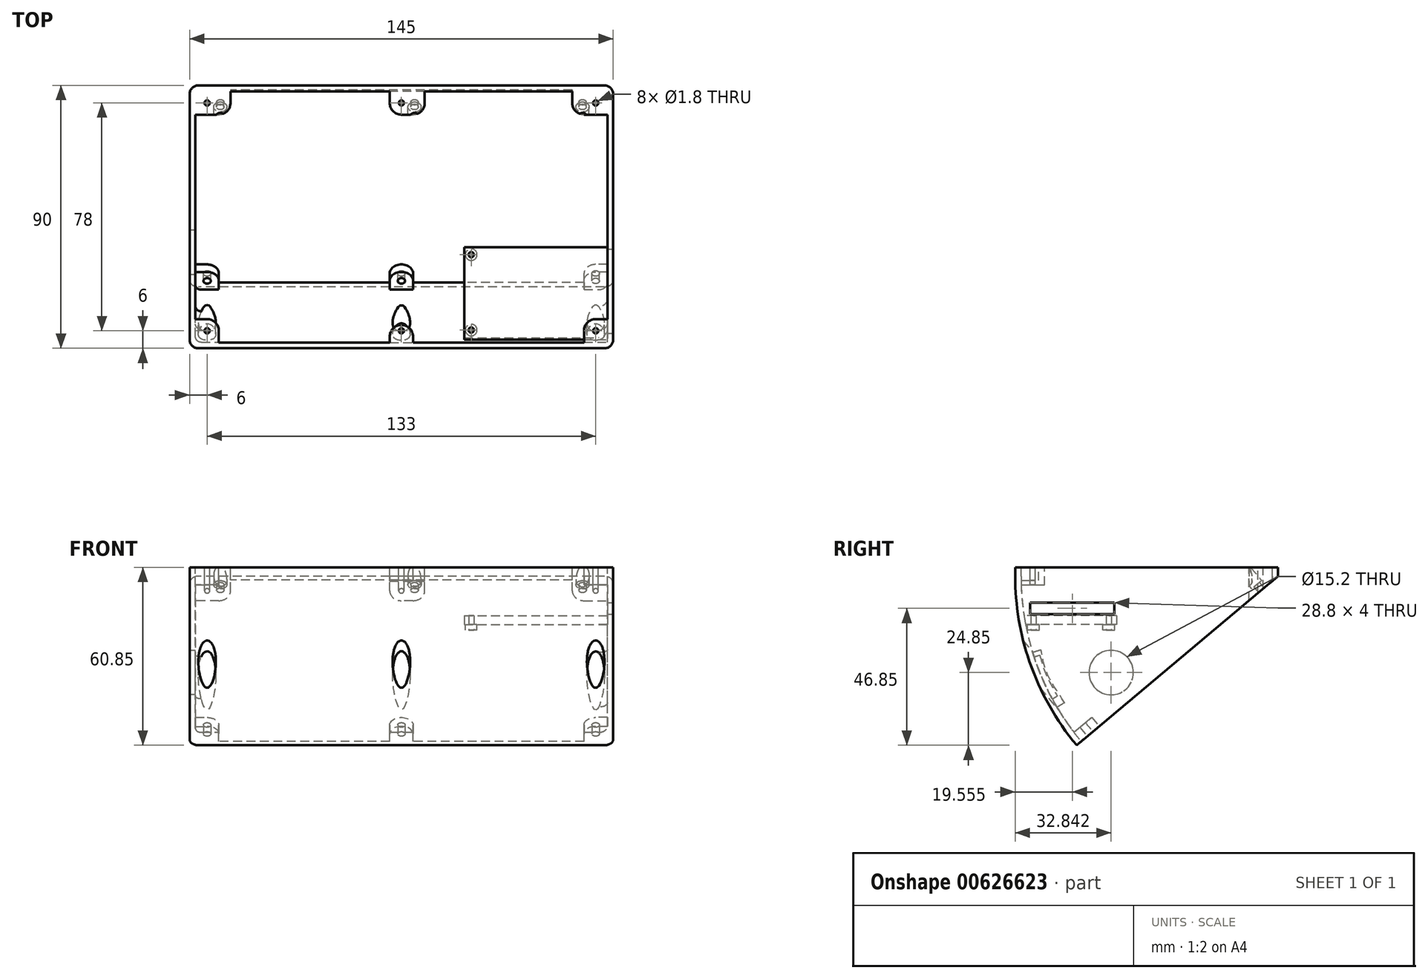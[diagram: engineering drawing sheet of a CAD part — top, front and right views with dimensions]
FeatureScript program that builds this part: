
annotation { "Feature Type Name" : "Feature", "Feature Type Description" : "" }
export const myFeature = defineFeature(function(context is Context, id is Id, definition is map)
    precondition{}
    {
        {
            var Q0;
            Q0=qCreatedBy(makeId("Top.planeOp"),FACE);
            var sketch = newSketch(context, id + "F0", { "sketchPlane" : qUnion([Q0])});
            skLineSegment(sketch, "E0.bottom", {"start": v(72.5, -45) * mm, "end": v(-72.5, -45) * mm});
            skLineSegment(sketch, "E0.top", {"start": v(72.5, 45) * mm, "end": v(-72.5, 45) * mm});
            skLineSegment(sketch, "E0.left", {"start": v(72.5, -45) * mm, "end": v(72.5, 45) * mm});
            skLineSegment(sketch, "E0.right", {"start": v(-72.5, -45) * mm, "end": v(-72.5, 45) * mm});
            skPoint(sketch, "E0.middle", {"position": v(0, 0) * mm});
            skLineSegment(sketch, "E1.bottom", {"start": v(70.5, -43) * mm, "end": v(-70.5, -43) * mm});
            skLineSegment(sketch, "E1.top", {"start": v(70.5, 43) * mm, "end": v(-70.5, 43) * mm});
            skLineSegment(sketch, "E1.left", {"start": v(70.5, -43) * mm, "end": v(70.5, 43) * mm});
            skLineSegment(sketch, "E1.right", {"start": v(-70.5, -43) * mm, "end": v(-70.5, 43) * mm});
            skSolve(sketch);
        }
        {
            var Q0;
            Q0=qCreatedBy(makeId("Right.planeOp"),FACE);
            cPlane(context, id + "F1", {"entities" : qUnion([Q0]), "cplaneType" : CPlaneType.OFFSET, "offset" : 75 * mm, "width" : 150 * mm, "height" : 150 * mm});
        }
        {
            var Q0;
            Q0=qCreatedBy(id+"F1.planeOp",FACE);
            var sketch = newSketch(context, id + "F2", { "sketchPlane" : qUnion([Q0])});
            skLineSegment(sketch, "E2", {"start": v(45, 0) * mm, "end": v(-16.28, -51.42) * mm, "construction": true});
            skArc(sketch, "E3", {"start": v(-35, 0) * mm, "mid": v(-30.18, -27.36) * mm, "end": v(-16.28, -51.42) * mm});
            skSolve(sketch);
        }
        {
            var Q0;
            Q0=makeQuery(id+"F0.imprint","IMPRINT",FACE,{"disambiguationData":[TD([[makeQuery(id+"F0.imprint","IMPRINT",EDGE,{"derivedFrom":sQuery(id+"F0.wireOp",EDGE,"E0.bottom")}),-1.0]])]});
            var Q1;
            Q1=sQuery(id+"F2.wireOp",EDGE,"E3");
            sweep(context, id + "F3", {"profiles" : qUnion([Q0]), "path" : qUnion([Q1])});
        }
        {
            var Q0;
            Q0=makeQuery(id+"F3.opSweep","CAP_FACE",FACE,{"disambiguationData":[OSD([sQuery(id+"F0.wireOp",EDGE,"E0.bottom"),sQuery(id+"F0.wireOp",EDGE,"E0.top"),sQuery(id+"F0.wireOp",EDGE,"E0.left"),sQuery(id+"F0.wireOp",EDGE,"E0.right"),sQuery(id+"F0.wireOp",EDGE,"E1.bottom"),sQuery(id+"F0.wireOp",EDGE,"E1.top"),sQuery(id+"F0.wireOp",EDGE,"E1.left"),sQuery(id+"F0.wireOp",EDGE,"E1.right"),sQuery(id+"F2.wireOp",VERTEX,"E3.start")])],"isStart":true});
            extrude(context, id + "F4", {"entities" : qUnion([Q0]), "operationType" : NewBodyOperationType.ADD, "depth" : 3 * mm});
        }
        {
            var Q0;
            {var subQ0=sQuery(id+"F0.wireOp",EDGE,"E0.right");Q0=makeQuery(id+"F4.boolean.opBoolean","MERGE",FACE,{"derivedFrom":[makeQuery(id+"F3.opSweep","SWEPT_FACE",FACE,{"disambiguationData":[OSD([subQ0,sQuery(id+"F2.wireOp",EDGE,"E3")])]}),makeQuery(id+"F4.opExtrude","SWEPT_FACE",FACE,{"disambiguationData":[OSD([subQ0,sQuery(id+"F2.wireOp",VERTEX,"E3.start")])]})]});}
            var sketch = newSketch(context, id + "F5", { "sketchPlane" : qUnion([Q0])});
            skCircle(sketch, "E4", {"center": v(12.16, -33) * mm, "radius": 7.6 * mm});
            skLineSegment(sketch, "E5", {"start": v(-45, 0) * mm, "end": v(12.16, -33) * mm, "construction": true});
            skCircle(sketch, "E6", {"center": v(12.16, -33) * mm, "radius": 9.5 * mm, "construction": true});
            skSolve(sketch);
        }
        {
            var Q0;
            Q0=makeQuery(id+"F5.imprint","IMPRINT",FACE,{"disambiguationData":[TD([[makeQuery(id+"F5.imprint","IMPRINT",EDGE,{"derivedFrom":sQuery(id+"F5.wireOp",EDGE,"E4")}),1.0]])]});
            extrude(context, id + "F6", {"entities" : qUnion([Q0]), "operationType" : NewBodyOperationType.REMOVE, "endBound" : BoundingType.UP_TO_NEXT, "oppositeDirection" : true, "depth" : 25 * mm});
        }
        {
            var Q0;
            {var subQ0=sQuery(id+"F0.wireOp",EDGE,"E0.left");Q0=makeQuery(id+"F4.boolean.opBoolean","MERGE",FACE,{"derivedFrom":[makeQuery(id+"F3.opSweep","SWEPT_FACE",FACE,{"disambiguationData":[OSD([subQ0,sQuery(id+"F2.wireOp",EDGE,"E3")])]}),makeQuery(id+"F4.opExtrude","SWEPT_FACE",FACE,{"disambiguationData":[OSD([subQ0,sQuery(id+"F2.wireOp",VERTEX,"E3.start")])]})]});}
            var sketch = newSketch(context, id + "F7", { "sketchPlane" : qUnion([Q0])});
            skLineSegment(sketch, "E7.bottom", {"start": v(-39.84, -9) * mm, "end": v(-11.04, -9) * mm});
            skLineSegment(sketch, "E7.top", {"start": v(-39.84, -13) * mm, "end": v(-11.04, -13) * mm});
            skLineSegment(sketch, "E7.left", {"start": v(-39.84, -9) * mm, "end": v(-39.84, -13) * mm});
            skLineSegment(sketch, "E7.right", {"start": v(-11.04, -9) * mm, "end": v(-11.04, -13) * mm});
            skPoint(sketch, "E8", {"position": v(-25.44, -9) * mm});
            skSolve(sketch);
        }
        {
            var Q0;
            Q0=makeQuery(id+"F7.imprint","IMPRINT",FACE,{"disambiguationData":[TD([[makeQuery(id+"F7.imprint","IMPRINT",EDGE,{"derivedFrom":sQuery(id+"F7.wireOp",EDGE,"E7.bottom")}),-1.0]])]});
            extrude(context, id + "F8", {"entities" : qUnion([Q0]), "operationType" : NewBodyOperationType.REMOVE, "endBound" : BoundingType.UP_TO_NEXT, "oppositeDirection" : true, "depth" : 25 * mm});
        }
        {
            var Q0;
            {var subQ0=sQuery(id+"F0.wireOp",EDGE,"E1.left");Q0=makeQuery(id+"F4.boolean.opBoolean","MERGE",FACE,{"derivedFrom":[makeQuery(id+"F3.opSweep","SWEPT_FACE",FACE,{"disambiguationData":[OSD([subQ0,sQuery(id+"F2.wireOp",EDGE,"E3")])]}),makeQuery(id+"F4.opExtrude","SWEPT_FACE",FACE,{"disambiguationData":[OSD([subQ0,sQuery(id+"F2.wireOp",VERTEX,"E3.start")])]})]});}
            var sketch = newSketch(context, id + "F9", { "sketchPlane" : qUnion([Q0])});
            skLineSegment(sketch, "E9.bottom", {"start": v(10.34, -13.5) * mm, "end": v(41.34, -13.5) * mm});
            skLineSegment(sketch, "E9.top", {"start": v(10.34, -16.5) * mm, "end": v(41.34, -16.5) * mm});
            skLineSegment(sketch, "E9.left", {"start": v(10.34, -13.5) * mm, "end": v(10.34, -16.5) * mm});
            skLineSegment(sketch, "E9.right", {"start": v(41.34, -13.5) * mm, "end": v(41.34, -16.5) * mm});
            skPoint(sketch, "E10", {"position": v(25.84, -13.5) * mm});
            skSolve(sketch);
        }
        {
            var Q0;
            Q0=makeQuery(id+"F9.imprint","IMPRINT",FACE,{"disambiguationData":[TD([[makeQuery(id+"F9.imprint","IMPRINT",EDGE,{"derivedFrom":sQuery(id+"F9.wireOp",EDGE,"E9.top")}),1.0]])]});
            extrude(context, id + "F10", {"entities" : qUnion([Q0]), "operationType" : NewBodyOperationType.ADD, "depth" : 49 * mm});
        }
        {
            var Q0;
            Q0=makeQuery(id+"F10.opExtrude","SWEPT_FACE",FACE,{"disambiguationData":[OSD([sQuery(id+"F9.wireOp",EDGE,"E9.top")])]});
            var sketch = newSketch(context, id + "F11", { "sketchPlane" : qUnion([Q0])});
            skCircle(sketch, "E11", {"center": v(23.9, 12.94) * mm, "radius": 0.9 * mm});
            skCircle(sketch, "E12", {"center": v(23.9, 38.74) * mm, "radius": 0.9 * mm});
            skLineSegment(sketch, "E13", {"start": v(21.5, 25.84) * mm, "end": v(33.65, 25.84) * mm, "construction": true});
            skCircle(sketch, "E14", {"center": v(23.9, 12.94) * mm, "radius": 2 * mm});
            skCircle(sketch, "E15", {"center": v(23.9, 38.74) * mm, "radius": 2 * mm});
            skSolve(sketch);
        }
        {
            var Q0;
            Q0=makeQuery(id+"F11.imprint","IMPRINT",FACE,{"disambiguationData":[TD([[makeQuery(id+"F11.imprint","IMPRINT",EDGE,{"derivedFrom":sQuery(id+"F11.wireOp",EDGE,"E12")}),1.0]])]});
            var Q1;
            Q1=makeQuery(id+"F11.imprint","IMPRINT",FACE,{"disambiguationData":[TD([[makeQuery(id+"F11.imprint","IMPRINT",EDGE,{"derivedFrom":sQuery(id+"F11.wireOp",EDGE,"E11")}),1.0]])]});
            extrude(context, id + "F12", {"entities" : qUnion([Q0, Q1]), "operationType" : NewBodyOperationType.REMOVE, "endBound" : BoundingType.UP_TO_NEXT, "oppositeDirection" : true, "depth" : 25 * mm});
        }
        {
            var Q0;
            Q0=makeQuery(id+"F11.imprint","IMPRINT",FACE,{"disambiguationData":[TD([[makeQuery(id+"F11.imprint","IMPRINT",EDGE,{"derivedFrom":sQuery(id+"F11.wireOp",EDGE,"E11")}),-1.0]])]});
            var Q1;
            Q1=makeQuery(id+"F11.imprint","IMPRINT",FACE,{"disambiguationData":[TD([[makeQuery(id+"F11.imprint","IMPRINT",EDGE,{"derivedFrom":sQuery(id+"F11.wireOp",EDGE,"E12")}),-1.0]])]});
            extrude(context, id + "F13", {"entities" : qUnion([Q0, Q1]), "operationType" : NewBodyOperationType.ADD, "depth" : 2 * mm});
        }
        {
            var Q0;
            Q0=makeQuery(id+"F10.opExtrude","SWEPT_FACE",FACE,{"disambiguationData":[OSD([sQuery(id+"F9.wireOp",EDGE,"E9.right")])]});
            var Q1;
            Q1=makeQuery(id+"F3.opSweep","SWEPT_FACE",FACE,{"disambiguationData":[OSD([sQuery(id+"F0.wireOp",EDGE,"E1.bottom"),sQuery(id+"F2.wireOp",EDGE,"E3")])]});
            extrude(context, id + "F14", {"entities" : qUnion([Q0]), "operationType" : NewBodyOperationType.ADD, "endBound" : BoundingType.UP_TO_SURFACE, "endBoundEntityFace" : qUnion([Q1]), "depth" : 25 * mm});
        }
        {
            var Q0;
            Q0=makeQuery(id+"F4.opExtrude","CAP_FACE",FACE,{"disambiguationData":[OSD([sQuery(id+"F0.wireOp",EDGE,"E0.bottom"),sQuery(id+"F0.wireOp",EDGE,"E0.top"),sQuery(id+"F0.wireOp",EDGE,"E0.left"),sQuery(id+"F0.wireOp",EDGE,"E0.right"),sQuery(id+"F0.wireOp",EDGE,"E1.bottom"),sQuery(id+"F0.wireOp",EDGE,"E1.top"),sQuery(id+"F0.wireOp",EDGE,"E1.left"),sQuery(id+"F0.wireOp",EDGE,"E1.right"),sQuery(id+"F2.wireOp",VERTEX,"E3.start")])],"isStart":false});
            var sketch = newSketch(context, id + "F15", { "sketchPlane" : qUnion([Q0])});
            skLineSegment(sketch, "E16.bottom", {"start": v(-70.5, -43) * mm, "end": v(-62.5, -43) * mm});
            skLineSegment(sketch, "E16.top", {"start": v(-70.5, -35) * mm, "end": v(-62.5, -35) * mm});
            skLineSegment(sketch, "E16.left", {"start": v(-70.5, -43) * mm, "end": v(-70.5, -35) * mm});
            skLineSegment(sketch, "E16.right", {"start": v(-62.5, -43) * mm, "end": v(-62.5, -35) * mm});
            skLineSegment(sketch, "E17.bottom", {"start": v(70.5, -43) * mm, "end": v(62.5, -43) * mm});
            skLineSegment(sketch, "E17.top", {"start": v(70.5, -35) * mm, "end": v(62.5, -35) * mm});
            skLineSegment(sketch, "E17.left", {"start": v(70.5, -43) * mm, "end": v(70.5, -35) * mm});
            skLineSegment(sketch, "E17.right", {"start": v(62.5, -43) * mm, "end": v(62.5, -35) * mm});
            skLineSegment(sketch, "E18.bottom", {"start": v(-70.5, 43) * mm, "end": v(-58.5, 43) * mm});
            skLineSegment(sketch, "E18.top", {"start": v(-70.5, 35) * mm, "end": v(-58.5, 35) * mm});
            skLineSegment(sketch, "E18.left", {"start": v(-70.5, 43) * mm, "end": v(-70.5, 35) * mm});
            skLineSegment(sketch, "E18.right", {"start": v(-58.5, 43) * mm, "end": v(-58.5, 35) * mm});
            skLineSegment(sketch, "E19.bottom", {"start": v(70.5, 43) * mm, "end": v(58.5, 43) * mm});
            skLineSegment(sketch, "E19.top", {"start": v(70.5, 35) * mm, "end": v(58.5, 35) * mm});
            skLineSegment(sketch, "E19.left", {"start": v(70.5, 43) * mm, "end": v(70.5, 35) * mm});
            skLineSegment(sketch, "E19.right", {"start": v(58.5, 43) * mm, "end": v(58.5, 35) * mm});
            skLineSegment(sketch, "E20.bottom", {"start": v(4, -43) * mm, "end": v(-4, -43) * mm});
            skLineSegment(sketch, "E20.top", {"start": v(4, -37) * mm, "end": v(-4, -37) * mm});
            skLineSegment(sketch, "E20.left", {"start": v(4, -43) * mm, "end": v(4, -37) * mm});
            skLineSegment(sketch, "E20.right", {"start": v(-4, -43) * mm, "end": v(-4, -37) * mm});
            skPoint(sketch, "E20.middle", {"position": v(0, -40) * mm});
            skLineSegment(sketch, "E21.bottom", {"start": v(-4, 43) * mm, "end": v(8, 43) * mm});
            skLineSegment(sketch, "E21.top", {"start": v(-4, 35) * mm, "end": v(8, 35) * mm});
            skLineSegment(sketch, "E21.left", {"start": v(-4, 43) * mm, "end": v(-4, 35) * mm});
            skLineSegment(sketch, "E21.right", {"start": v(8, 43) * mm, "end": v(8, 35) * mm});
            skSolve(sketch);
        }
        {
            var Q0;
            Q0=makeQuery(id+"F15.imprint","IMPRINT",FACE,{"disambiguationData":[TD([[makeQuery(id+"F15.imprint","IMPRINT",EDGE,{"derivedFrom":sQuery(id+"F15.wireOp",EDGE,"E16.bottom")}),-1.0]])]});
            var Q1;
            Q1=makeQuery(id+"F15.imprint","IMPRINT",FACE,{"disambiguationData":[TD([[makeQuery(id+"F15.imprint","IMPRINT",EDGE,{"derivedFrom":sQuery(id+"F15.wireOp",EDGE,"E17.bottom")}),-1.0]])]});
            extrude(context, id + "F16", {"entities" : qUnion([Q0, Q1]), "operationType" : NewBodyOperationType.ADD, "oppositeDirection" : true, "depth" : 6 * mm});
        }
        {
            var Q0;
            Q0=makeQuery(id+"F15.imprint","IMPRINT",FACE,{"disambiguationData":[TD([[makeQuery(id+"F15.imprint","IMPRINT",EDGE,{"derivedFrom":sQuery(id+"F15.wireOp",EDGE,"E20.bottom")}),-1.0]])]});
            extrude(context, id + "F17", {"entities" : qUnion([Q0]), "operationType" : NewBodyOperationType.ADD, "oppositeDirection" : true, "depth" : 4.5 * mm});
        }
        {
            var Q0;
            Q0=makeQuery(id+"F15.imprint","IMPRINT",FACE,{"disambiguationData":[TD([[makeQuery(id+"F15.imprint","IMPRINT",EDGE,{"derivedFrom":sQuery(id+"F15.wireOp",EDGE,"E18.bottom")}),1.0]])]});
            var Q1;
            Q1=makeQuery(id+"F15.imprint","IMPRINT",FACE,{"disambiguationData":[TD([[makeQuery(id+"F15.imprint","IMPRINT",EDGE,{"derivedFrom":sQuery(id+"F15.wireOp",EDGE,"E19.bottom")}),1.0]])]});
            var Q2;
            Q2=makeQuery(id+"F15.imprint","IMPRINT",FACE,{"disambiguationData":[TD([[makeQuery(id+"F15.imprint","IMPRINT",EDGE,{"derivedFrom":sQuery(id+"F15.wireOp",EDGE,"E21.bottom")}),1.0]])]});
            var Q3;
            Q3=makeQuery(id+"F3.opSweep","CAP_FACE",FACE,{"disambiguationData":[OSD([sQuery(id+"F0.wireOp",EDGE,"E0.bottom"),sQuery(id+"F0.wireOp",EDGE,"E0.top"),sQuery(id+"F0.wireOp",EDGE,"E0.left"),sQuery(id+"F0.wireOp",EDGE,"E0.right"),sQuery(id+"F0.wireOp",EDGE,"E1.bottom"),sQuery(id+"F0.wireOp",EDGE,"E1.top"),sQuery(id+"F0.wireOp",EDGE,"E1.left"),sQuery(id+"F0.wireOp",EDGE,"E1.right"),sQuery(id+"F2.wireOp",VERTEX,"E3.end")])],"isStart":false});
            extrude(context, id + "F18", {"entities" : qUnion([Q0, Q1, Q2]), "operationType" : NewBodyOperationType.ADD, "endBound" : BoundingType.UP_TO_SURFACE, "oppositeDirection" : true, "endBoundEntityFace" : qUnion([Q3]), "depth" : 25 * mm});
        }
        {
            var Q0;
            {var subQ2=sQuery(id+"F0.wireOp",EDGE,"E1.left");var subQ9=sQuery(id+"F15.wireOp",EDGE,"E19.bottom");var subQ10=sQuery(id+"F2.wireOp",EDGE,"E3");Q0=makeQuery(id+"F18.boolean.opBoolean","SPLIT",FACE,{"disambiguationData":[TD([makeQuery(id+"F18.opExtrude","SWEPT_FACE",FACE,{"disambiguationData":[OSD([subQ9])]})])],"derivedFrom":makeQuery(id+"F4.boolean.opBoolean","MERGE",FACE,{"derivedFrom":[makeQuery(id+"F3.opSweep","SWEPT_FACE",FACE,{"disambiguationData":[OSD([subQ2,subQ10])]}),makeQuery(id+"F4.opExtrude","SWEPT_FACE",FACE,{"disambiguationData":[OSD([subQ2,sQuery(id+"F2.wireOp",VERTEX,"E3.start")])]})]})});}
            var Q1;
            Q1=makeQuery(id+"F18.opExtrude","SWEPT_FACE",FACE,{"disambiguationData":[OSD([sQuery(id+"F15.wireOp",EDGE,"E19.right")])]});
            extrude(context, id + "F19", {"entities" : qUnion([Q0]), "operationType" : NewBodyOperationType.ADD, "endBound" : BoundingType.UP_TO_SURFACE, "endBoundEntityFace" : qUnion([Q1]), "depth" : 25 * mm});
        }
        {
            var Q0;
            {var subQ0=sQuery(id+"F15.wireOp",EDGE,"E18.bottom");var subQ2=sQuery(id+"F0.wireOp",EDGE,"E1.right");var subQ10=sQuery(id+"F2.wireOp",EDGE,"E3");Q0=makeQuery(id+"F18.boolean.opBoolean","SPLIT",FACE,{"disambiguationData":[TD([makeQuery(id+"F18.opExtrude","SWEPT_FACE",FACE,{"disambiguationData":[OSD([subQ0])]})])],"derivedFrom":makeQuery(id+"F4.boolean.opBoolean","MERGE",FACE,{"derivedFrom":[makeQuery(id+"F3.opSweep","SWEPT_FACE",FACE,{"disambiguationData":[OSD([subQ2,subQ10])]}),makeQuery(id+"F4.opExtrude","SWEPT_FACE",FACE,{"disambiguationData":[OSD([subQ2,sQuery(id+"F2.wireOp",VERTEX,"E3.start")])]})]})});}
            var Q1;
            Q1=makeQuery(id+"F18.opExtrude","SWEPT_FACE",FACE,{"disambiguationData":[OSD([sQuery(id+"F15.wireOp",EDGE,"E18.right")])]});
            extrude(context, id + "F20", {"entities" : qUnion([Q0]), "operationType" : NewBodyOperationType.ADD, "endBound" : BoundingType.UP_TO_SURFACE, "endBoundEntityFace" : qUnion([Q1]), "depth" : 25 * mm});
        }
        {
            var Q0;
            Q0=makeQuery(id+"F18.boolean.opBoolean","MERGE",FACE,{"derivedFrom":[makeQuery(id+"F16.boolean.opBoolean","MERGE",FACE,{"derivedFrom":[makeQuery(id+"F4.opExtrude","CAP_FACE",FACE,{"disambiguationData":[OSD([sQuery(id+"F0.wireOp",EDGE,"E0.bottom"),sQuery(id+"F0.wireOp",EDGE,"E0.top"),sQuery(id+"F0.wireOp",EDGE,"E0.left"),sQuery(id+"F0.wireOp",EDGE,"E0.right"),sQuery(id+"F0.wireOp",EDGE,"E1.bottom"),sQuery(id+"F0.wireOp",EDGE,"E1.top"),sQuery(id+"F0.wireOp",EDGE,"E1.left"),sQuery(id+"F0.wireOp",EDGE,"E1.right"),sQuery(id+"F2.wireOp",VERTEX,"E3.start")])],"isStart":false}),makeQuery(id+"F16.opExtrude","CAP_FACE",FACE,{"disambiguationData":[OSD([sQuery(id+"F15.wireOp",EDGE,"E16.bottom"),sQuery(id+"F15.wireOp",EDGE,"E16.top"),sQuery(id+"F15.wireOp",EDGE,"E16.left"),sQuery(id+"F15.wireOp",EDGE,"E16.right")])],"isStart":true}),makeQuery(id+"F16.opExtrude","CAP_FACE",FACE,{"disambiguationData":[OSD([sQuery(id+"F15.wireOp",EDGE,"E17.bottom"),sQuery(id+"F15.wireOp",EDGE,"E17.top"),sQuery(id+"F15.wireOp",EDGE,"E17.left"),sQuery(id+"F15.wireOp",EDGE,"E17.right")])],"isStart":true})]}),makeQuery(id+"F18.opExtrude","CAP_FACE",FACE,{"disambiguationData":[OSD([sQuery(id+"F15.wireOp",EDGE,"E18.bottom"),sQuery(id+"F15.wireOp",EDGE,"E18.top"),sQuery(id+"F15.wireOp",EDGE,"E18.left"),sQuery(id+"F15.wireOp",EDGE,"E18.right")])],"isStart":true}),makeQuery(id+"F18.opExtrude","CAP_FACE",FACE,{"disambiguationData":[OSD([sQuery(id+"F15.wireOp",EDGE,"E19.bottom"),sQuery(id+"F15.wireOp",EDGE,"E19.top"),sQuery(id+"F15.wireOp",EDGE,"E19.left"),sQuery(id+"F15.wireOp",EDGE,"E19.right")])],"isStart":true})]});
            var sketch = newSketch(context, id + "F21", { "sketchPlane" : qUnion([Q0])});
            skCircle(sketch, "E22", {"center": v(-66.5, 39) * mm, "radius": 0.9 * mm});
            skCircle(sketch, "E23", {"center": v(-66.5, -39) * mm, "radius": 0.9 * mm});
            skCircle(sketch, "E24", {"center": v(66.5, -39) * mm, "radius": 0.9 * mm});
            skCircle(sketch, "E25", {"center": v(66.5, 39) * mm, "radius": 0.9 * mm});
            skCircle(sketch, "E26", {"center": v(0, -39) * mm, "radius": 0.9 * mm});
            skCircle(sketch, "E27", {"center": v(0, 39) * mm, "radius": 0.9 * mm});
            skSolve(sketch);
        }
        {
            var Q0;
            Q0=makeQuery(id+"F21.imprint","IMPRINT",FACE,{"disambiguationData":[TD([[makeQuery(id+"F21.imprint","IMPRINT",EDGE,{"derivedFrom":sQuery(id+"F21.wireOp",EDGE,"E23")}),1.0]])]});
            var Q1;
            Q1=makeQuery(id+"F21.imprint","IMPRINT",FACE,{"disambiguationData":[TD([[makeQuery(id+"F21.imprint","IMPRINT",EDGE,{"derivedFrom":sQuery(id+"F21.wireOp",EDGE,"E24")}),1.0]])]});
            var Q2;
            Q2=makeQuery(id+"F21.imprint","IMPRINT",FACE,{"disambiguationData":[TD([[makeQuery(id+"F21.imprint","IMPRINT",EDGE,{"derivedFrom":sQuery(id+"F21.wireOp",EDGE,"E25")}),1.0]])]});
            var Q3;
            Q3=makeQuery(id+"F21.imprint","IMPRINT",FACE,{"disambiguationData":[TD([[makeQuery(id+"F21.imprint","IMPRINT",EDGE,{"derivedFrom":sQuery(id+"F21.wireOp",EDGE,"E22")}),1.0]])]});
            var Q4;
            Q4=makeQuery(id+"F21.imprint","IMPRINT",FACE,{"disambiguationData":[TD([[makeQuery(id+"F21.imprint","IMPRINT",EDGE,{"derivedFrom":sQuery(id+"F21.wireOp",EDGE,"E26")}),1.0]])]});
            var Q5;
            Q5=makeQuery(id+"F21.imprint","IMPRINT",FACE,{"disambiguationData":[TD([[makeQuery(id+"F21.imprint","IMPRINT",EDGE,{"derivedFrom":sQuery(id+"F21.wireOp",EDGE,"E27")}),1.0]])]});
            extrude(context, id + "F22", {"entities" : qUnion([Q0, Q1, Q2, Q3, Q4, Q5]), "operationType" : NewBodyOperationType.REMOVE, "endBound" : BoundingType.UP_TO_NEXT, "oppositeDirection" : true, "depth" : 25 * mm});
        }
        {
            var Q0;
            {var subQ0=sQuery(id+"F2.wireOp",VERTEX,"E3.end");var subQ1=sQuery(id+"F0.wireOp",EDGE,"E1.right");var subQ2=sQuery(id+"F0.wireOp",EDGE,"E1.left");var subQ3=sQuery(id+"F0.wireOp",EDGE,"E1.top");var subQ4=sQuery(id+"F0.wireOp",EDGE,"E1.bottom");var subQ5=sQuery(id+"F0.wireOp",EDGE,"E0.right");var subQ6=sQuery(id+"F0.wireOp",EDGE,"E0.left");var subQ7=sQuery(id+"F0.wireOp",EDGE,"E0.top");var subQ8=sQuery(id+"F0.wireOp",EDGE,"E0.bottom");Q0=makeQuery(id+"F20.boolean.opBoolean","MERGE",FACE,{"derivedFrom":[makeQuery(id+"F19.boolean.opBoolean","MERGE",FACE,{"derivedFrom":[makeQuery(id+"F18.boolean.opBoolean","MERGE",FACE,{"derivedFrom":[makeQuery(id+"F3.opSweep","CAP_FACE",FACE,{"disambiguationData":[OSD([subQ8,subQ7,subQ6,subQ5,subQ4,subQ3,subQ2,subQ1,subQ0])],"isStart":false}),makeQuery(id+"F18.opExtrude","CAP_FACE",FACE,{"disambiguationData":[OSD([subQ8,subQ7,subQ6,subQ5,subQ4,subQ3,subQ2,subQ1,subQ0]),ownerDisambiguation([makeQuery(id+"F15.imprint","IMPRINT",EDGE,{"derivedFrom":sQuery(id+"F15.wireOp",EDGE,"E18.bottom")})])],"isStart":false}),makeQuery(id+"F18.opExtrude","CAP_FACE",FACE,{"disambiguationData":[OSD([subQ8,subQ7,subQ6,subQ5,subQ4,subQ3,subQ2,subQ1,subQ0]),ownerDisambiguation([makeQuery(id+"F15.imprint","IMPRINT",EDGE,{"derivedFrom":sQuery(id+"F15.wireOp",EDGE,"E19.bottom")})])],"isStart":false})]}),makeQuery(id+"F19.opExtrude","SWEPT_FACE",FACE,{"disambiguationData":[OSD([subQ2,subQ0])]})]}),makeQuery(id+"F20.opExtrude","SWEPT_FACE",FACE,{"disambiguationData":[OSD([subQ1,subQ0])]})]});}
            var sketch = newSketch(context, id + "F23", { "sketchPlane" : qUnion([Q0])});
            skLineSegment(sketch, "E28.bottom", {"start": v(-70.5, 53.53) * mm, "end": v(-62.5, 53.53) * mm});
            skLineSegment(sketch, "E28.top", {"start": v(-70.5, 45.53) * mm, "end": v(-62.5, 45.53) * mm});
            skLineSegment(sketch, "E28.left", {"start": v(-70.5, 53.53) * mm, "end": v(-70.5, 45.53) * mm});
            skLineSegment(sketch, "E28.right", {"start": v(-62.5, 53.53) * mm, "end": v(-62.5, 45.53) * mm});
            skLineSegment(sketch, "E29.bottom", {"start": v(70.5, 53.53) * mm, "end": v(62.5, 53.53) * mm});
            skLineSegment(sketch, "E29.top", {"start": v(70.5, 45.53) * mm, "end": v(62.5, 45.53) * mm});
            skLineSegment(sketch, "E29.left", {"start": v(70.5, 53.53) * mm, "end": v(70.5, 45.53) * mm});
            skLineSegment(sketch, "E29.right", {"start": v(62.5, 53.53) * mm, "end": v(62.5, 45.53) * mm});
            skLineSegment(sketch, "E30", {"start": v(70.5, 53.53) * mm, "end": v(62.5, 45.53) * mm, "construction": true});
            skLineSegment(sketch, "E31", {"start": v(-70.5, 53.53) * mm, "end": v(-62.5, 45.53) * mm, "construction": true});
            skLineSegment(sketch, "E32.bottom", {"start": v(-4, 53.53) * mm, "end": v(4, 53.53) * mm});
            skLineSegment(sketch, "E32.top", {"start": v(-4, 45.53) * mm, "end": v(4, 45.53) * mm});
            skLineSegment(sketch, "E32.left", {"start": v(-4, 53.53) * mm, "end": v(-4, 45.53) * mm});
            skLineSegment(sketch, "E32.right", {"start": v(4, 53.53) * mm, "end": v(4, 45.53) * mm});
            skPoint(sketch, "E32.middle", {"position": v(0, 49.53) * mm});
            skPoint(sketch, "E32.middle.positionSnap0", {"position": v(0, 53.53) * mm});
            skPoint(sketch, "E32.centerSnap0", {"position": v(0, 53.53) * mm});
            skSolve(sketch);
        }
        {
            var Q0;
            Q0=makeQuery(id+"F23.imprint","IMPRINT",FACE,{"disambiguationData":[TD([[makeQuery(id+"F23.imprint","IMPRINT",EDGE,{"derivedFrom":sQuery(id+"F23.wireOp",EDGE,"E28.bottom")}),1.0]])]});
            var Q1;
            Q1=makeQuery(id+"F23.imprint","IMPRINT",FACE,{"disambiguationData":[TD([[makeQuery(id+"F23.imprint","IMPRINT",EDGE,{"derivedFrom":sQuery(id+"F23.wireOp",EDGE,"E29.bottom")}),1.0]])]});
            var Q2;
            Q2=makeQuery(id+"F23.imprint","IMPRINT",FACE,{"disambiguationData":[TD([[makeQuery(id+"F23.imprint","IMPRINT",EDGE,{"derivedFrom":sQuery(id+"F23.wireOp",EDGE,"E32.bottom")}),1.0]])]});
            extrude(context, id + "F24", {"entities" : qUnion([Q0, Q1, Q2]), "operationType" : NewBodyOperationType.ADD, "oppositeDirection" : true, "depth" : 4 * mm});
        }
        {
            var Q0;
            {var subQ0=sQuery(id+"F2.wireOp",VERTEX,"E3.end");var subQ1=sQuery(id+"F0.wireOp",EDGE,"E1.right");var subQ2=sQuery(id+"F0.wireOp",EDGE,"E1.left");var subQ3=sQuery(id+"F0.wireOp",EDGE,"E1.top");var subQ4=sQuery(id+"F0.wireOp",EDGE,"E1.bottom");var subQ5=sQuery(id+"F0.wireOp",EDGE,"E0.right");var subQ6=sQuery(id+"F0.wireOp",EDGE,"E0.left");var subQ7=sQuery(id+"F0.wireOp",EDGE,"E0.top");var subQ8=sQuery(id+"F0.wireOp",EDGE,"E0.bottom");Q0=makeQuery(id+"F24.boolean.opBoolean","MERGE",FACE,{"derivedFrom":[makeQuery(id+"F20.boolean.opBoolean","MERGE",FACE,{"derivedFrom":[makeQuery(id+"F19.boolean.opBoolean","MERGE",FACE,{"derivedFrom":[makeQuery(id+"F18.boolean.opBoolean","MERGE",FACE,{"derivedFrom":[makeQuery(id+"F3.opSweep","CAP_FACE",FACE,{"disambiguationData":[OSD([subQ8,subQ7,subQ6,subQ5,subQ4,subQ3,subQ2,subQ1,subQ0])],"isStart":false}),makeQuery(id+"F18.opExtrude","CAP_FACE",FACE,{"disambiguationData":[OSD([subQ8,subQ7,subQ6,subQ5,subQ4,subQ3,subQ2,subQ1,subQ0]),ownerDisambiguation([makeQuery(id+"F15.imprint","IMPRINT",EDGE,{"derivedFrom":sQuery(id+"F15.wireOp",EDGE,"E18.bottom")})])],"isStart":false}),makeQuery(id+"F18.opExtrude","CAP_FACE",FACE,{"disambiguationData":[OSD([subQ8,subQ7,subQ6,subQ5,subQ4,subQ3,subQ2,subQ1,subQ0]),ownerDisambiguation([makeQuery(id+"F15.imprint","IMPRINT",EDGE,{"derivedFrom":sQuery(id+"F15.wireOp",EDGE,"E19.bottom")})])],"isStart":false})]}),makeQuery(id+"F19.opExtrude","SWEPT_FACE",FACE,{"disambiguationData":[OSD([subQ2,subQ0])]})]}),makeQuery(id+"F20.opExtrude","SWEPT_FACE",FACE,{"disambiguationData":[OSD([subQ1,subQ0])]})]}),makeQuery(id+"F24.opExtrude","CAP_FACE",FACE,{"disambiguationData":[OSD([sQuery(id+"F23.wireOp",EDGE,"E28.bottom"),sQuery(id+"F23.wireOp",EDGE,"E28.top"),sQuery(id+"F23.wireOp",EDGE,"E28.left"),sQuery(id+"F23.wireOp",EDGE,"E28.right")])],"isStart":true}),makeQuery(id+"F24.opExtrude","CAP_FACE",FACE,{"disambiguationData":[OSD([sQuery(id+"F23.wireOp",EDGE,"E29.bottom"),sQuery(id+"F23.wireOp",EDGE,"E29.top"),sQuery(id+"F23.wireOp",EDGE,"E29.left"),sQuery(id+"F23.wireOp",EDGE,"E29.right")])],"isStart":true})]});}
            var sketch = newSketch(context, id + "F25", { "sketchPlane" : qUnion([Q0])});
            skCircle(sketch, "E33", {"center": v(-66.5, 49.53) * mm, "radius": 1.25 * mm});
            skPoint(sketch, "E33.centerSnap0", {"position": v(-62.5, 49.53) * mm});
            skPoint(sketch, "E33.centerSnap1", {"position": v(-66.5, 45.53) * mm});
            skCircle(sketch, "E34", {"center": v(66.5, 49.53) * mm, "radius": 1.25 * mm});
            skPoint(sketch, "E34.centerSnap0", {"position": v(66.5, 45.53) * mm});
            skPoint(sketch, "E34.centerSnap1", {"position": v(62.5, 49.53) * mm});
            skCircle(sketch, "E35", {"center": v(66.5, 49.53) * mm, "radius": 3 * mm});
            skCircle(sketch, "E36", {"center": v(-66.5, 49.53) * mm, "radius": 3 * mm});
            skCircle(sketch, "E37", {"center": v(62, -26.94) * mm, "radius": 1.25 * mm});
            skCircle(sketch, "E38", {"center": v(-62, -26.94) * mm, "radius": 1.25 * mm});
            skPoint(sketch, "E39", {"position": v(58.5, -26.94) * mm});
            skPoint(sketch, "E40", {"position": v(-58.5, -26.94) * mm});
            skCircle(sketch, "E41", {"center": v(62, -26.94) * mm, "radius": 2.25 * mm});
            skCircle(sketch, "E42", {"center": v(-62, -26.94) * mm, "radius": 2.25 * mm});
            skCircle(sketch, "E43", {"center": v(4.5, -26.94) * mm, "radius": 1.25 * mm});
            skCircle(sketch, "E44", {"center": v(4.5, -26.94) * mm, "radius": 2.25 * mm});
            skCircle(sketch, "E45", {"center": v(0, 49.53) * mm, "radius": 1.25 * mm});
            skCircle(sketch, "E46", {"center": v(0, 49.53) * mm, "radius": 3 * mm});
            skSolve(sketch);
        }
        {
            var Q0;
            Q0=makeQuery(id+"F25.imprint","IMPRINT",FACE,{"disambiguationData":[TD([[makeQuery(id+"F25.imprint","IMPRINT",EDGE,{"derivedFrom":sQuery(id+"F25.wireOp",EDGE,"E33")}),1.0]])]});
            var Q1;
            Q1=makeQuery(id+"F25.imprint","IMPRINT",FACE,{"disambiguationData":[TD([[makeQuery(id+"F25.imprint","IMPRINT",EDGE,{"derivedFrom":sQuery(id+"F25.wireOp",EDGE,"E34")}),1.0]])]});
            var Q2;
            Q2=makeQuery(id+"F25.imprint","IMPRINT",FACE,{"disambiguationData":[TD([[makeQuery(id+"F25.imprint","IMPRINT",EDGE,{"derivedFrom":sQuery(id+"F25.wireOp",EDGE,"E45")}),1.0]])]});
            extrude(context, id + "F26", {"entities" : qUnion([Q0, Q1, Q2]), "operationType" : NewBodyOperationType.REMOVE, "endBound" : BoundingType.THROUGH_ALL, "oppositeDirection" : true, "depth" : 25 * mm});
        }
        {
            var Q0;
            Q0=makeQuery(id+"F25.imprint","IMPRINT",FACE,{"disambiguationData":[TD([[makeQuery(id+"F25.imprint","IMPRINT",EDGE,{"derivedFrom":sQuery(id+"F25.wireOp",EDGE,"E34")}),-1.0]])]});
            var Q1;
            Q1=makeQuery(id+"F25.imprint","IMPRINT",FACE,{"disambiguationData":[TD([[makeQuery(id+"F25.imprint","IMPRINT",EDGE,{"derivedFrom":sQuery(id+"F25.wireOp",EDGE,"E33")}),-1.0]])]});
            var Q2;
            Q2=makeQuery(id+"F25.imprint","IMPRINT",FACE,{"disambiguationData":[TD([[makeQuery(id+"F25.imprint","IMPRINT",EDGE,{"derivedFrom":sQuery(id+"F25.wireOp",EDGE,"E45")}),-1.0]])]});
            extrude(context, id + "F27", {"entities" : qUnion([Q0, Q1, Q2]), "operationType" : NewBodyOperationType.REMOVE, "endBound" : BoundingType.THROUGH_ALL, "oppositeDirection" : true, "depth" : 25 * mm, "hasSecondDirection" : true, "secondDirectionOppositeDirection" : true, "secondDirectionDepth" : 4 * mm});
        }
        {
            var Q0;
            Q0=makeQuery(id+"F25.imprint","IMPRINT",FACE,{"disambiguationData":[TD([[makeQuery(id+"F25.imprint","IMPRINT",EDGE,{"derivedFrom":sQuery(id+"F25.wireOp",EDGE,"E38")}),1.0]])]});
            var Q1;
            Q1=makeQuery(id+"F25.imprint","IMPRINT",FACE,{"disambiguationData":[TD([[makeQuery(id+"F25.imprint","IMPRINT",EDGE,{"derivedFrom":sQuery(id+"F25.wireOp",EDGE,"E37")}),1.0]])]});
            var Q2;
            Q2=makeQuery(id+"F25.imprint","IMPRINT",FACE,{"disambiguationData":[TD([[makeQuery(id+"F25.imprint","IMPRINT",EDGE,{"derivedFrom":sQuery(id+"F25.wireOp",EDGE,"E43")}),1.0]])]});
            extrude(context, id + "F28", {"entities" : qUnion([Q0, Q1, Q2]), "operationType" : NewBodyOperationType.REMOVE, "endBound" : BoundingType.UP_TO_NEXT, "oppositeDirection" : true, "depth" : 25 * mm});
        }
        {
            var Q0;
            Q0=makeQuery(id+"F25.imprint","IMPRINT",FACE,{"disambiguationData":[TD([[makeQuery(id+"F25.imprint","IMPRINT",EDGE,{"derivedFrom":sQuery(id+"F25.wireOp",EDGE,"E38")}),-1.0]])]});
            var Q1;
            Q1=makeQuery(id+"F25.imprint","IMPRINT",FACE,{"disambiguationData":[TD([[makeQuery(id+"F25.imprint","IMPRINT",EDGE,{"derivedFrom":sQuery(id+"F25.wireOp",EDGE,"E37")}),-1.0]])]});
            var Q2;
            Q2=makeQuery(id+"F25.imprint","IMPRINT",FACE,{"disambiguationData":[TD([[makeQuery(id+"F25.imprint","IMPRINT",EDGE,{"derivedFrom":sQuery(id+"F25.wireOp",EDGE,"E43")}),-1.0]])]});
            extrude(context, id + "F29", {"entities" : qUnion([Q0, Q1, Q2]), "operationType" : NewBodyOperationType.REMOVE, "endBound" : BoundingType.UP_TO_NEXT, "oppositeDirection" : true, "depth" : 25 * mm, "hasSecondDirection" : true, "secondDirectionOppositeDirection" : true, "secondDirectionDepth" : 2.5 * mm});
        }
        {
            var Q0;
            Q0=makeQuery(id+"F18.opExtrude","SWEPT_EDGE",EDGE,{"disambiguationData":[OSD([sQuery(id+"F15.wireOp",EDGE,"E18.top"),sQuery(id+"F15.wireOp",EDGE,"E18.right")])]});
            var Q1;
            Q1=makeQuery(id+"F16.opExtrude","SWEPT_EDGE",EDGE,{"disambiguationData":[OSD([sQuery(id+"F15.wireOp",EDGE,"E16.top"),sQuery(id+"F15.wireOp",EDGE,"E16.right")])]});
            var Q2;
            Q2=makeQuery(id+"F16.opExtrude","SWEPT_EDGE",EDGE,{"disambiguationData":[OSD([sQuery(id+"F15.wireOp",EDGE,"E17.top"),sQuery(id+"F15.wireOp",EDGE,"E17.right")])]});
            var Q3;
            Q3=makeQuery(id+"F18.opExtrude","SWEPT_EDGE",EDGE,{"disambiguationData":[OSD([sQuery(id+"F15.wireOp",EDGE,"E19.top"),sQuery(id+"F15.wireOp",EDGE,"E19.right")])]});
            var Q4;
            Q4=makeQuery(id+"F24.opExtrude","SWEPT_EDGE",EDGE,{"disambiguationData":[OSD([sQuery(id+"F23.wireOp",EDGE,"E29.top"),sQuery(id+"F23.wireOp",EDGE,"E29.right")])]});
            var Q5;
            Q5=makeQuery(id+"F24.opExtrude","SWEPT_EDGE",EDGE,{"disambiguationData":[OSD([sQuery(id+"F23.wireOp",EDGE,"E28.top"),sQuery(id+"F23.wireOp",EDGE,"E28.right")])]});
            var Q6;
            Q6=makeQuery(id+"F16.opExtrude","SWEPT_EDGE",EDGE,{"disambiguationData":[OSD([sQuery(id+"F15.wireOp",EDGE,"E20.top"),sQuery(id+"F15.wireOp",EDGE,"E20.right")])]});
            var Q7;
            Q7=makeQuery(id+"F16.opExtrude","SWEPT_EDGE",EDGE,{"disambiguationData":[OSD([sQuery(id+"F15.wireOp",EDGE,"E20.top"),sQuery(id+"F15.wireOp",EDGE,"E20.left")])]});
            var Q8;
            Q8=makeQuery(id+"F18.opExtrude","SWEPT_EDGE",EDGE,{"disambiguationData":[OSD([sQuery(id+"F15.wireOp",EDGE,"E21.top"),sQuery(id+"F15.wireOp",EDGE,"E21.left")])]});
            var Q9;
            Q9=makeQuery(id+"F18.opExtrude","SWEPT_EDGE",EDGE,{"disambiguationData":[OSD([sQuery(id+"F15.wireOp",EDGE,"E21.top"),sQuery(id+"F15.wireOp",EDGE,"E21.right")])]});
            var Q10;
            Q10=makeQuery(id+"F24.opExtrude","SWEPT_EDGE",EDGE,{"disambiguationData":[OSD([sQuery(id+"F23.wireOp",EDGE,"E32.top"),sQuery(id+"F23.wireOp",EDGE,"E32.right")])]});
            var Q11;
            Q11=makeQuery(id+"F24.opExtrude","SWEPT_EDGE",EDGE,{"disambiguationData":[OSD([sQuery(id+"F23.wireOp",EDGE,"E32.top"),sQuery(id+"F23.wireOp",EDGE,"E32.left")])]});
            var Q12;
            Q12=makeQuery(id+"F17.opExtrude","SWEPT_EDGE",EDGE,{"disambiguationData":[OSD([sQuery(id+"F15.wireOp",EDGE,"E20.top"),sQuery(id+"F15.wireOp",EDGE,"E20.left")])]});
            var Q13;
            Q13=makeQuery(id+"F17.opExtrude","SWEPT_EDGE",EDGE,{"disambiguationData":[OSD([sQuery(id+"F15.wireOp",EDGE,"E20.top"),sQuery(id+"F15.wireOp",EDGE,"E20.right")])]});
            fillet(context, id + "F30", {"entities" : qUnion([Q0, Q1, Q2, Q3, Q4, Q5, Q6, Q7, Q8, Q9, Q10, Q11, Q12, Q13]), "radius" : 4 * mm, "tangentPropagation" : true, "allowEdgeOverflow" : false});
        }
        {
            var Q0;
            Q0=makeQuery(id+"F4.opExtrude","SWEPT_EDGE",EDGE,{"disambiguationData":[OSD([sQuery(id+"F0.wireOp",EDGE,"E0.top"),sQuery(id+"F0.wireOp",EDGE,"E0.right")])]});
            var Q1;
            Q1=makeQuery(id+"F3.opSweep","SWEPT_EDGE",EDGE,{"disambiguationData":[OSD([sQuery(id+"F0.wireOp",EDGE,"E0.bottom"),sQuery(id+"F0.wireOp",EDGE,"E0.right"),sQuery(id+"F2.wireOp",EDGE,"E3")])]});
            var Q2;
            Q2=makeQuery(id+"F3.opSweep","SWEPT_EDGE",EDGE,{"disambiguationData":[OSD([sQuery(id+"F0.wireOp",EDGE,"E0.bottom"),sQuery(id+"F0.wireOp",EDGE,"E0.left"),sQuery(id+"F2.wireOp",EDGE,"E3")])]});
            var Q3;
            Q3=makeQuery(id+"F4.opExtrude","SWEPT_EDGE",EDGE,{"disambiguationData":[OSD([sQuery(id+"F0.wireOp",EDGE,"E0.top"),sQuery(id+"F0.wireOp",EDGE,"E0.left")])]});
            var Q4;
            {var subQ0=sQuery(id+"F0.wireOp",EDGE,"E1.left");var subQ1=sQuery(id+"F2.wireOp",EDGE,"E3");var subQ2=sQuery(id+"F0.wireOp",EDGE,"E1.bottom");var subQ3=sQuery(id+"F9.wireOp",EDGE,"E9.top");Q4=makeQuery(id+"F14.boolean.opBoolean","SPLIT",EDGE,{"disambiguationData":[TD([makeQuery(id+"F10.opExtrude","SWEPT_FACE",FACE,{"disambiguationData":[OSD([subQ3])]})])],"derivedFrom":makeQuery(id+"F3.opSweep","SWEPT_EDGE",EDGE,{"disambiguationData":[OSD([subQ2,subQ0,subQ1])]})});}
            fillet(context, id + "F31", {"entities" : qUnion([Q0, Q1, Q2, Q3, Q4]), "radius" : 3 * mm, "tangentPropagation" : true, "allowEdgeOverflow" : false});
        }
        {
            var Q0;
            Q0=makeQuery(id+"F3.opSweep","SWEPT_EDGE",EDGE,{"disambiguationData":[OSD([sQuery(id+"F0.wireOp",EDGE,"E1.bottom"),sQuery(id+"F0.wireOp",EDGE,"E1.right"),sQuery(id+"F2.wireOp",EDGE,"E3")])]});
            fillet(context, id + "F32", {"entities" : qUnion([Q0]), "radius" : 2 * mm, "tangentPropagation" : true, "allowEdgeOverflow" : false});
        }
    });
